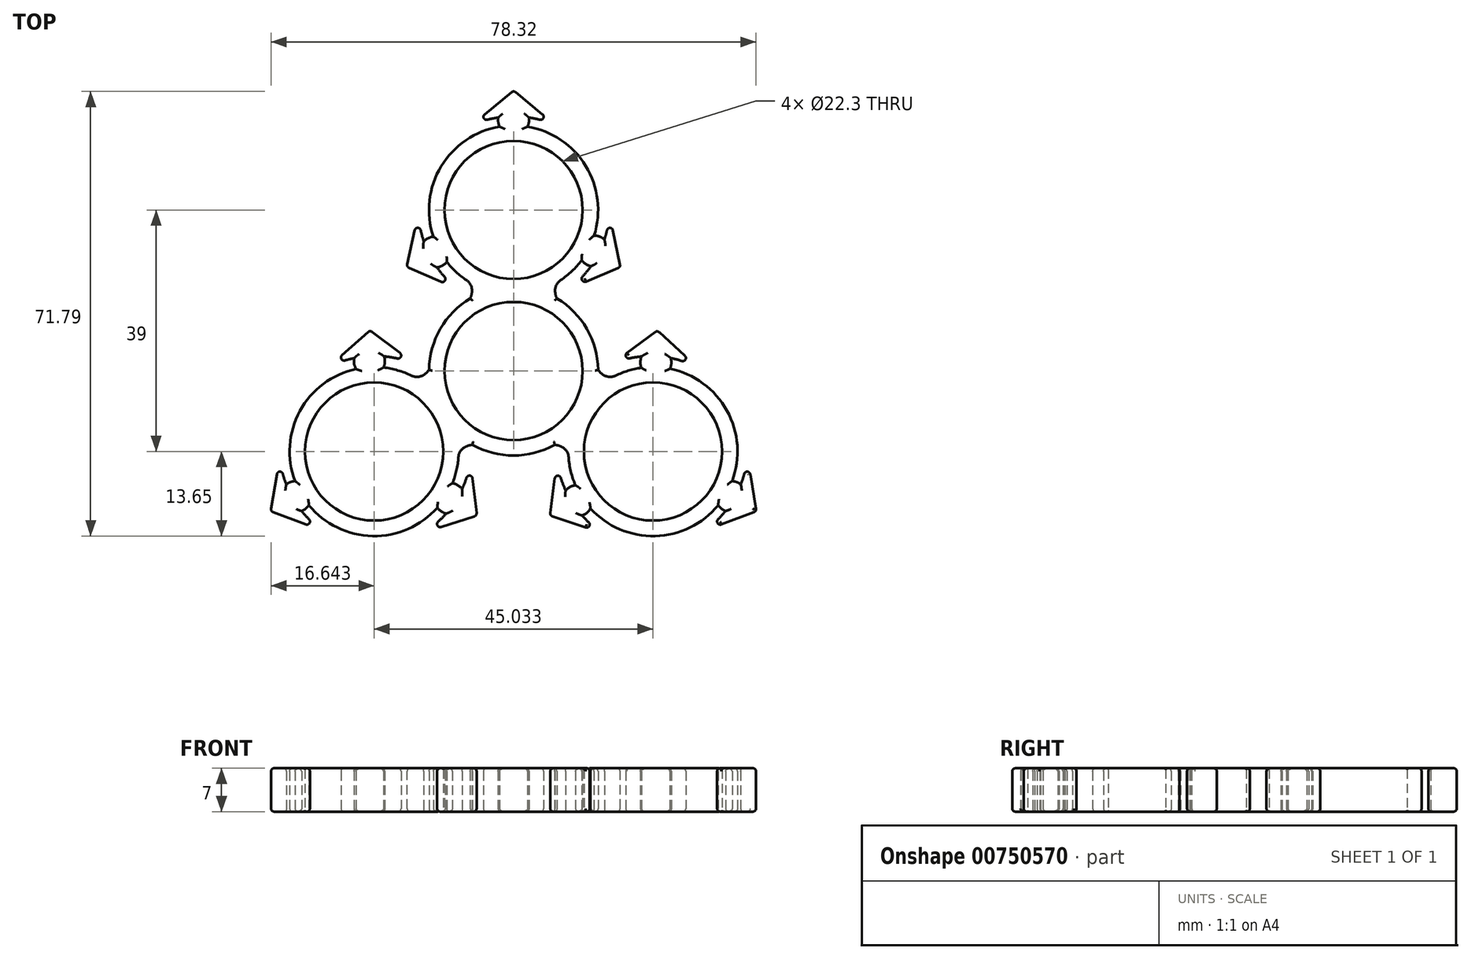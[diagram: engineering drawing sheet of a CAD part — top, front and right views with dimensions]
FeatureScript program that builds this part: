
annotation { "Feature Type Name" : "Feature", "Feature Type Description" : "" }
export const myFeature = defineFeature(function(context is Context, id is Id, definition is map)
    precondition{}
    {
        {
            var Q0;
            Q0=qCreatedBy(makeId("Top.planeOp"),FACE);
            var sketch = newSketch(context, id + "F0", { "sketchPlane" : qUnion([Q0])});
            skCircle(sketch, "E0", {"center": v(0, 0) * mm, "radius": 11.15 * mm});
            skArc(sketch, "E1.0", {"start": v(-5.17, 12.63) * mm, "mid": v(-6.92, 11.76) * mm, "end": v(-8.53, 10.66) * mm, "construction": true});
            skLineSegment(sketch, "E2", {"start": v(0, 0) * mm, "end": v(0, 26) * mm, "construction": true});
            skCircle(sketch, "E3", {"center": v(0, 26) * mm, "radius": 11.15 * mm});
            skArc(sketch, "E4.0", {"start": v(7, 14.28) * mm, "mid": v(0, 39.65) * mm, "end": v(-7, 14.28) * mm});
            skPoint(sketch, "E5.visualSharp", {"position": v(0, 16.7) * mm});
            skLineSegment(sketch, "E6.0", {"start": v(7, 0) * mm, "end": v(7, 29.5) * mm, "construction": true});
            skArc(sketch, "E7.trimOffspring", {"start": v(-7, 11.72) * mm, "mid": v(0, -13.65) * mm, "end": v(7, 11.72) * mm});
            skArc(sketch, "E8", {"start": v(7, 14.28) * mm, "mid": v(6.7, 13) * mm, "end": v(7, 11.72) * mm});
            skArc(sketch, "E9.MirrorCS", {"start": v(-7, 14.28) * mm, "mid": v(-6.7, 13) * mm, "end": v(-7, 11.72) * mm});
            skLineSegment(sketch, "E10", {"start": v(0, 45.29) * mm, "end": v(-6.95, 39.57) * mm});
            skPoint(sketch, "E10.startSnap0", {"position": v(0, 39.65) * mm});
            skLineSegment(sketch, "E11", {"start": v(0, 45.29) * mm, "end": v(6.95, 39.57) * mm});
            skArc(sketch, "E12", {"start": v(6.95, 39.57) * mm, "mid": v(0, 41.13) * mm, "end": v(-6.95, 39.57) * mm});
            skLineSegment(sketch, "E13", {"start": v(17.28, 16.78) * mm, "end": v(15.47, 25.6) * mm});
            skLineSegment(sketch, "E14", {"start": v(17.28, 16.78) * mm, "end": v(8.97, 13.3) * mm});
            skArc(sketch, "E15", {"start": v(8.97, 13.3) * mm, "mid": v(13.6, 18.72) * mm, "end": v(15.47, 25.6) * mm});
            skLineSegment(sketch, "E16", {"start": v(-17.26, 16.8) * mm, "end": v(-9, 13.23) * mm});
            skLineSegment(sketch, "E17", {"start": v(-17.26, 16.8) * mm, "end": v(-15.34, 25.6) * mm});
            skArc(sketch, "E18", {"start": v(-15.34, 25.6) * mm, "mid": v(-13.56, 18.7) * mm, "end": v(-9, 13.23) * mm});
            skCircle(sketch, "E19", {"center": v(0, 40.55) * mm, "radius": 2.5 * mm});
            skCircle(sketch, "E20", {"center": v(13.01, 19.37) * mm, "radius": 2.5 * mm});
            skCircle(sketch, "E21", {"center": v(-12.69, 19.2) * mm, "radius": 2.5 * mm});
            skSolve(sketch);
        }
        {
            var Q0;
            Q0=qSketchRegion(id+"F2",true);
            var Q1;
            Q1=qSketchRegion(id+"F0",true);
            var Q2;
            {var subQ0=sQuery(id+"F0.wireOp",EDGE,"5286eaf0-ed28-4451-94e3-1d908ec19ca7");var subQ1=sQuery(id+"F0.wireOp",EDGE,"E3");var subQ2=makeQuery(id+"F0.imprint","INTERSECT",VERTEX,{"disambiguationData":[OD(0.0)],"derivedFrom":[subQ1,subQ0]});Q2=makeQuery(id+"F0.imprint","IMPRINT",FACE,{"disambiguationData":[TD([[makeQuery(id+"F0.imprint","IMPRINT",EDGE,{"disambiguationData":[TD([[subQ2,-1.0]])],"derivedFrom":subQ1}),-1.0]])]});}
            var Q3;
            {var subQ0=sQuery(id+"F0.wireOp",EDGE,"972e2314-292c-46cc-950a-d2e98ffed2b1");var subQ1=sQuery(id+"F0.wireOp",EDGE,"E3");var subQ2=makeQuery(id+"F0.imprint","INTERSECT",VERTEX,{"disambiguationData":[OD(0.0)],"derivedFrom":[subQ1,subQ0]});Q3=makeQuery(id+"F0.imprint","IMPRINT",FACE,{"disambiguationData":[TD([[makeQuery(id+"F0.imprint","IMPRINT",EDGE,{"disambiguationData":[TD([[subQ2,-1.0]])],"derivedFrom":subQ1}),-1.0]])]});}
            var Q4;
            {var subQ0=sQuery(id+"F0.wireOp",EDGE,"8576df35-fd95-4b7d-8476-f7b5d8a5ebd1");var subQ1=sQuery(id+"F0.wireOp",EDGE,"E3");var subQ2=makeQuery(id+"F0.imprint","INTERSECT",VERTEX,{"disambiguationData":[OD(0.0)],"derivedFrom":[subQ1,subQ0]});Q4=makeQuery(id+"F0.imprint","IMPRINT",FACE,{"disambiguationData":[TD([[makeQuery(id+"F0.imprint","IMPRINT",EDGE,{"disambiguationData":[TD([[subQ2,-1.0]])],"derivedFrom":subQ1}),-1.0]])]});}
            var Q5;
            {var subQ0=sQuery(id+"F0.wireOp",EDGE,"upsWoKqN-qIG4-cDSa-tKJD-hM69GbnP515O");var subQ1=sQuery(id+"F0.wireOp",EDGE,"E3");var subQ2=makeQuery(id+"F0.imprint","INTERSECT",VERTEX,{"disambiguationData":[OD(0.0)],"derivedFrom":[subQ1,subQ0]});Q5=makeQuery(id+"F0.imprint","IMPRINT",FACE,{"disambiguationData":[TD([[makeQuery(id+"F0.imprint","IMPRINT",EDGE,{"disambiguationData":[TD([[subQ2,-1.0]])],"derivedFrom":subQ1}),-1.0]])]});}
            var Q6;
            {var subQ0=sQuery(id+"F0.wireOp",EDGE,"2dc68220-ebba-422f-adc0-bbb553f4a656");var subQ1=sQuery(id+"F0.wireOp",EDGE,"E3");var subQ2=makeQuery(id+"F0.imprint","INTERSECT",VERTEX,{"disambiguationData":[OD(0.0)],"derivedFrom":[subQ1,subQ0]});Q6=makeQuery(id+"F0.imprint","IMPRINT",FACE,{"disambiguationData":[TD([[makeQuery(id+"F0.imprint","IMPRINT",EDGE,{"disambiguationData":[TD([[subQ2,-1.0]])],"derivedFrom":subQ1}),-1.0]])]});}
            var Q7;
            {var subQ0=sQuery(id+"F0.wireOp",EDGE,"70cbc2a9-83ff-4b48-bb73-ff75b1e053e5");var subQ1=sQuery(id+"F0.wireOp",EDGE,"E3");var subQ2=makeQuery(id+"F0.imprint","INTERSECT",VERTEX,{"disambiguationData":[OD(0.0)],"derivedFrom":[subQ1,subQ0]});Q7=makeQuery(id+"F0.imprint","IMPRINT",FACE,{"disambiguationData":[TD([[makeQuery(id+"F0.imprint","IMPRINT",EDGE,{"disambiguationData":[TD([[subQ2,1.0]])],"derivedFrom":subQ1}),-1.0]])]});}
            var Q8;
            {var subQ0=sQuery(id+"F0.wireOp",EDGE,"8457dc48-e8ce-439c-b6e1-438fe0c9034f");var subQ1=sQuery(id+"F0.wireOp",EDGE,"E3");var subQ2=makeQuery(id+"F0.imprint","INTERSECT",VERTEX,{"disambiguationData":[OD(0.0)],"derivedFrom":[subQ1,subQ0]});Q8=makeQuery(id+"F0.imprint","IMPRINT",FACE,{"disambiguationData":[TD([[makeQuery(id+"F0.imprint","IMPRINT",EDGE,{"disambiguationData":[TD([[subQ2,-1.0]])],"derivedFrom":subQ1}),-1.0]])]});}
            var Q9;
            {var subQ0=sQuery(id+"F0.wireOp",EDGE,"6db5ce6a-88a4-4cba-8603-f791245f7d5f");var subQ1=sQuery(id+"F0.wireOp",EDGE,"E3");var subQ2=makeQuery(id+"F0.imprint","INTERSECT",VERTEX,{"disambiguationData":[OD(0.0)],"derivedFrom":[subQ1,subQ0]});Q9=makeQuery(id+"F0.imprint","IMPRINT",FACE,{"disambiguationData":[TD([[makeQuery(id+"F0.imprint","IMPRINT",EDGE,{"disambiguationData":[TD([[subQ2,-1.0]])],"derivedFrom":subQ1}),-1.0]])]});}
            var Q10;
            {var subQ0=sQuery(id+"F0.wireOp",EDGE,"26ba9915-316d-43ac-97a0-efcd31670470");var subQ1=sQuery(id+"F0.wireOp",EDGE,"E3");var subQ2=makeQuery(id+"F0.imprint","INTERSECT",VERTEX,{"disambiguationData":[OD(0.0)],"derivedFrom":[subQ1,subQ0]});Q10=makeQuery(id+"F0.imprint","IMPRINT",FACE,{"disambiguationData":[TD([[makeQuery(id+"F0.imprint","IMPRINT",EDGE,{"disambiguationData":[TD([[subQ2,-1.0]])],"derivedFrom":subQ1}),-1.0]])]});}
            extrude(context, id + "F1", {"entities" : qUnion([Q0, Q1, Q2, Q3, Q4, Q5, Q6, Q7, Q8, Q9, Q10]), "depth" : 7 * mm, "offsetDistance" : 25 * mm});
        }
        {
            var Q0;
            Q0=qCreatedBy(makeId("Right.planeOp"),FACE);
            var sketch = newSketch(context, id + "F2", { "sketchPlane" : qUnion([Q0])});
            skLineSegment(sketch, "E22", {"start": v(0, -11.35) * mm, "end": v(0, 14.45) * mm, "construction": true});
            skSolve(sketch);
        }
        {
            var Q0;
            Q0=makeQuery(id+"F1.opExtrude","SWEPT_EDGE",EDGE,{"disambiguationData":[OSD([sQuery(id+"F0.wireOp",EDGE,"E4.0"),sQuery(id+"F0.wireOp",EDGE,"gXTc2K6m-pDrj-VkwX-DA3g-2FsoQV2dXgWA"),sQuery(id+"F0.wireOp",EDGE,"E8")])]});
            var Q1;
            Q1=makeQuery(id+"F1.opExtrude","SWEPT_EDGE",EDGE,{"disambiguationData":[OSD([sQuery(id+"F0.wireOp",EDGE,"E4.0"),sQuery(id+"F0.wireOp",EDGE,"WV1YJwpc-lhCt-Tkbw-pyGD-IAguLvoMxcio"),sQuery(id+"F0.wireOp",EDGE,"E9.MirrorCS")])]});
            fillet(context, id + "F3", {"entities" : qUnion([Q0, Q1]), "radius" : 2 * mm, "tangentPropagation" : true, "allowEdgeOverflow" : false});
        }
        {
            var Q0;
            Q0=makeQuery(id+"F1.opExtrude","SWEPT_FACE",FACE,{"disambiguationData":[OSD([sQuery(id+"F0.wireOp",EDGE,"E0")])]});
            var Q1;
            Q1=makeQuery(id+"F1.opExtrude","SWEPT_FACE",FACE,{"disambiguationData":[OSD([sQuery(id+"F0.wireOp",EDGE,"E3")])]});
            fillet(context, id + "F4", {"entities" : qUnion([Q0, Q1]), "radius" : 0.2 * mm, "tangentPropagation" : true, "allowEdgeOverflow" : false});
        }
        {
            var Q0;
            Q0=makeQuery(id+"F1.opExtrude","SWEPT_BODY",BODY,{"disambiguationData":[OSD([sQuery(id+"F0.wireOp",EDGE,"E0"),sQuery(id+"F0.wireOp",EDGE,"E1.0"),sQuery(id+"F0.wireOp",EDGE,"E3"),sQuery(id+"F0.wireOp",EDGE,"E4.0"),sQuery(id+"F0.wireOp",EDGE,"7c884c8c-e37f-41f7-9a8e-9150e4511ce8.0"),sQuery(id+"F0.wireOp",EDGE,"124d70be-8a2f-4ff1-8067-023c3a760d13.0"),sQuery(id+"F0.wireOp",EDGE,"7qioyo7K-iHsX-Xa6s-X97m-BwtuQXfGrCvp"),sQuery(id+"F0.wireOp",EDGE,"oFAU7C9Q-nsB6-dseo-MMuZ-7hNLlDQCrwbt"),sQuery(id+"F0.wireOp",EDGE,"a2486781-22df-47b1-8026-fe576fbc433f.0"),sQuery(id+"F0.wireOp",EDGE,"cb9c9ce2-17e4-408e-8bf5-b38f411324f0.0"),sQuery(id+"F0.wireOp",EDGE,"jKmUo85i-UXFQ-YKQP-mafa-QPdGbBQ2pSZu"),sQuery(id+"F0.wireOp",EDGE,"14rnQz0T-OoW9-SuH9-BmvN-4Fd0IeYT7QfG")])]});
            var Q1;
            Q1=sQuery(id+"F2.wireOp",EDGE,"E22");
            circularPattern(context, id + "F5", {"operationType" : NewBodyOperationType.ADD, "entities" : qUnion([Q0]), "axis" : qUnion([Q1]), "angle" : 360 * degree, "instanceCount" : 3, "equalSpace" : true});
        }
        {
            var Q0;
            {var subQ0=makeQuery(id+"F1.opExtrude","CAP_FACE",FACE,{"disambiguationData":[OSD([sQuery(id+"F0.wireOp",EDGE,"E0"),sQuery(id+"F0.wireOp",EDGE,"E3"),sQuery(id+"F0.wireOp",EDGE,"E4.0"),sQuery(id+"F0.wireOp",EDGE,"E7.trimOffspring"),sQuery(id+"F0.wireOp",EDGE,"E8"),sQuery(id+"F0.wireOp",EDGE,"E9.MirrorCS"),sQuery(id+"F0.wireOp",EDGE,"E10"),sQuery(id+"F0.wireOp",EDGE,"E11"),sQuery(id+"F0.wireOp",EDGE,"E12"),sQuery(id+"F0.wireOp",EDGE,"E13"),sQuery(id+"F0.wireOp",EDGE,"E14"),sQuery(id+"F0.wireOp",EDGE,"E15"),sQuery(id+"F0.wireOp",EDGE,"E16"),sQuery(id+"F0.wireOp",EDGE,"E17"),sQuery(id+"F0.wireOp",EDGE,"E18"),sQuery(id+"F0.wireOp",EDGE,"E19"),sQuery(id+"F0.wireOp",EDGE,"E20"),sQuery(id+"F0.wireOp",EDGE,"E21")])],"isStart":false});Q0=makeQuery(id+"F5.boolean.opBoolean","MERGE",FACE,{"derivedFrom":[subQ0,makeQuery(id+"F5.opPattern","COPY",FACE,{"derivedFrom":subQ0,"instanceName":"1"}),makeQuery(id+"F5.opPattern","COPY",FACE,{"derivedFrom":subQ0,"instanceName":"2"})]});}
            var Q1;
            {var subQ0=makeQuery(id+"F1.opExtrude","CAP_FACE",FACE,{"disambiguationData":[OSD([sQuery(id+"F0.wireOp",EDGE,"E0"),sQuery(id+"F0.wireOp",EDGE,"E3"),sQuery(id+"F0.wireOp",EDGE,"E4.0"),sQuery(id+"F0.wireOp",EDGE,"E7.trimOffspring"),sQuery(id+"F0.wireOp",EDGE,"E8"),sQuery(id+"F0.wireOp",EDGE,"E9.MirrorCS"),sQuery(id+"F0.wireOp",EDGE,"E10"),sQuery(id+"F0.wireOp",EDGE,"E11"),sQuery(id+"F0.wireOp",EDGE,"E12"),sQuery(id+"F0.wireOp",EDGE,"E13"),sQuery(id+"F0.wireOp",EDGE,"E14"),sQuery(id+"F0.wireOp",EDGE,"E15"),sQuery(id+"F0.wireOp",EDGE,"E16"),sQuery(id+"F0.wireOp",EDGE,"E17"),sQuery(id+"F0.wireOp",EDGE,"E18"),sQuery(id+"F0.wireOp",EDGE,"E19"),sQuery(id+"F0.wireOp",EDGE,"E20"),sQuery(id+"F0.wireOp",EDGE,"E21")])],"isStart":true});Q1=makeQuery(id+"F5.boolean.opBoolean","MERGE",FACE,{"derivedFrom":[subQ0,makeQuery(id+"F5.opPattern","COPY",FACE,{"derivedFrom":subQ0,"instanceName":"1"}),makeQuery(id+"F5.opPattern","COPY",FACE,{"derivedFrom":subQ0,"instanceName":"2"})]});}
            fillet(context, id + "F6", {"entities" : qUnion([Q0, Q1]), "radius" : .5 * mm, "tangentPropagation" : true, "allowEdgeOverflow" : false});
        }
        {
            var Q0;
            Q0=makeQuery(id+"F5.opPattern","COPY",EDGE,{"derivedFrom":makeQuery(id+"F1.opExtrude","SWEPT_EDGE",EDGE,{"disambiguationData":[OSD([sQuery(id+"F0.wireOp",EDGE,"E10"),sQuery(id+"F0.wireOp",EDGE,"E11")])]}),"instanceName":"1"});
            var Q1;
            Q1=makeQuery(id+"F5.opPattern","COPY",EDGE,{"derivedFrom":makeQuery(id+"F1.opExtrude","SWEPT_EDGE",EDGE,{"disambiguationData":[OSD([sQuery(id+"F0.wireOp",EDGE,"E10"),sQuery(id+"F0.wireOp",EDGE,"E12")])]}),"instanceName":"1"});
            var Q2;
            Q2=makeQuery(id+"F5.opPattern","COPY",EDGE,{"derivedFrom":makeQuery(id+"F1.opExtrude","SWEPT_EDGE",EDGE,{"disambiguationData":[OSD([sQuery(id+"F0.wireOp",EDGE,"E11"),sQuery(id+"F0.wireOp",EDGE,"E12")])]}),"instanceName":"1"});
            var Q3;
            Q3=makeQuery(id+"F5.opPattern","COPY",EDGE,{"derivedFrom":makeQuery(id+"F1.opExtrude","SWEPT_EDGE",EDGE,{"disambiguationData":[OSD([sQuery(id+"F0.wireOp",EDGE,"E16"),sQuery(id+"F0.wireOp",EDGE,"E18")])]}),"instanceName":"1"});
            var Q4;
            Q4=makeQuery(id+"F5.opPattern","COPY",EDGE,{"derivedFrom":makeQuery(id+"F1.opExtrude","SWEPT_EDGE",EDGE,{"disambiguationData":[OSD([sQuery(id+"F0.wireOp",EDGE,"E16"),sQuery(id+"F0.wireOp",EDGE,"E17")])]}),"instanceName":"1"});
            var Q5;
            Q5=makeQuery(id+"F5.opPattern","COPY",EDGE,{"derivedFrom":makeQuery(id+"F1.opExtrude","SWEPT_EDGE",EDGE,{"disambiguationData":[OSD([sQuery(id+"F0.wireOp",EDGE,"E17"),sQuery(id+"F0.wireOp",EDGE,"E18")])]}),"instanceName":"1"});
            var Q6;
            Q6=makeQuery(id+"F5.opPattern","COPY",FACE,{"derivedFrom":makeQuery(id+"F1.opExtrude","SWEPT_FACE",FACE,{"disambiguationData":[OSD([sQuery(id+"F0.wireOp",EDGE,"E13")])]}),"instanceName":"1"});
            var Q7;
            Q7=makeQuery(id+"F5.opPattern","COPY",FACE,{"derivedFrom":makeQuery(id+"F1.opExtrude","SWEPT_FACE",FACE,{"disambiguationData":[OSD([sQuery(id+"F0.wireOp",EDGE,"E14")])]}),"instanceName":"1"});
            var Q8;
            Q8=makeQuery(id+"F5.opPattern","COPY",FACE,{"derivedFrom":makeQuery(id+"F1.opExtrude","SWEPT_FACE",FACE,{"disambiguationData":[OSD([sQuery(id+"F0.wireOp",EDGE,"E14")])]}),"instanceName":"2"});
            var Q9;
            Q9=makeQuery(id+"F5.opPattern","COPY",FACE,{"derivedFrom":makeQuery(id+"F1.opExtrude","SWEPT_FACE",FACE,{"disambiguationData":[OSD([sQuery(id+"F0.wireOp",EDGE,"E13")])]}),"instanceName":"2"});
            var Q10;
            Q10=makeQuery(id+"F5.opPattern","COPY",FACE,{"derivedFrom":makeQuery(id+"F1.opExtrude","SWEPT_FACE",FACE,{"disambiguationData":[OSD([sQuery(id+"F0.wireOp",EDGE,"E11")])]}),"instanceName":"2"});
            var Q11;
            Q11=makeQuery(id+"F5.opPattern","COPY",FACE,{"derivedFrom":makeQuery(id+"F1.opExtrude","SWEPT_FACE",FACE,{"disambiguationData":[OSD([sQuery(id+"F0.wireOp",EDGE,"E10")])]}),"instanceName":"2"});
            var Q12;
            Q12=makeQuery(id+"F5.opPattern","COPY",FACE,{"derivedFrom":makeQuery(id+"F1.opExtrude","SWEPT_FACE",FACE,{"disambiguationData":[OSD([sQuery(id+"F0.wireOp",EDGE,"E17")])]}),"instanceName":"2"});
            var Q13;
            Q13=makeQuery(id+"F5.opPattern","COPY",FACE,{"derivedFrom":makeQuery(id+"F1.opExtrude","SWEPT_FACE",FACE,{"disambiguationData":[OSD([sQuery(id+"F0.wireOp",EDGE,"E16")])]}),"instanceName":"2"});
            var Q14;
            Q14=makeQuery(id+"F1.opExtrude","SWEPT_FACE",FACE,{"disambiguationData":[OSD([sQuery(id+"F0.wireOp",EDGE,"E13")])]});
            var Q15;
            Q15=makeQuery(id+"F1.opExtrude","SWEPT_FACE",FACE,{"disambiguationData":[OSD([sQuery(id+"F0.wireOp",EDGE,"E14")])]});
            var Q16;
            Q16=makeQuery(id+"F1.opExtrude","SWEPT_FACE",FACE,{"disambiguationData":[OSD([sQuery(id+"F0.wireOp",EDGE,"E11")])]});
            var Q17;
            Q17=makeQuery(id+"F1.opExtrude","SWEPT_FACE",FACE,{"disambiguationData":[OSD([sQuery(id+"F0.wireOp",EDGE,"E10")])]});
            var Q18;
            Q18=makeQuery(id+"F1.opExtrude","SWEPT_FACE",FACE,{"disambiguationData":[OSD([sQuery(id+"F0.wireOp",EDGE,"E17")])]});
            var Q19;
            Q19=makeQuery(id+"F1.opExtrude","SWEPT_FACE",FACE,{"disambiguationData":[OSD([sQuery(id+"F0.wireOp",EDGE,"E16")])]});
            fillet(context, id + "F7", {"entities" : qUnion([Q0, Q1, Q2, Q3, Q4, Q5, Q6, Q7, Q8, Q9, Q10, Q11, Q12, Q13, Q14, Q15, Q16, Q17, Q18, Q19]), "radius" : .5 * mm, "tangentPropagation" : true, "allowEdgeOverflow" : false});
        }
    });
